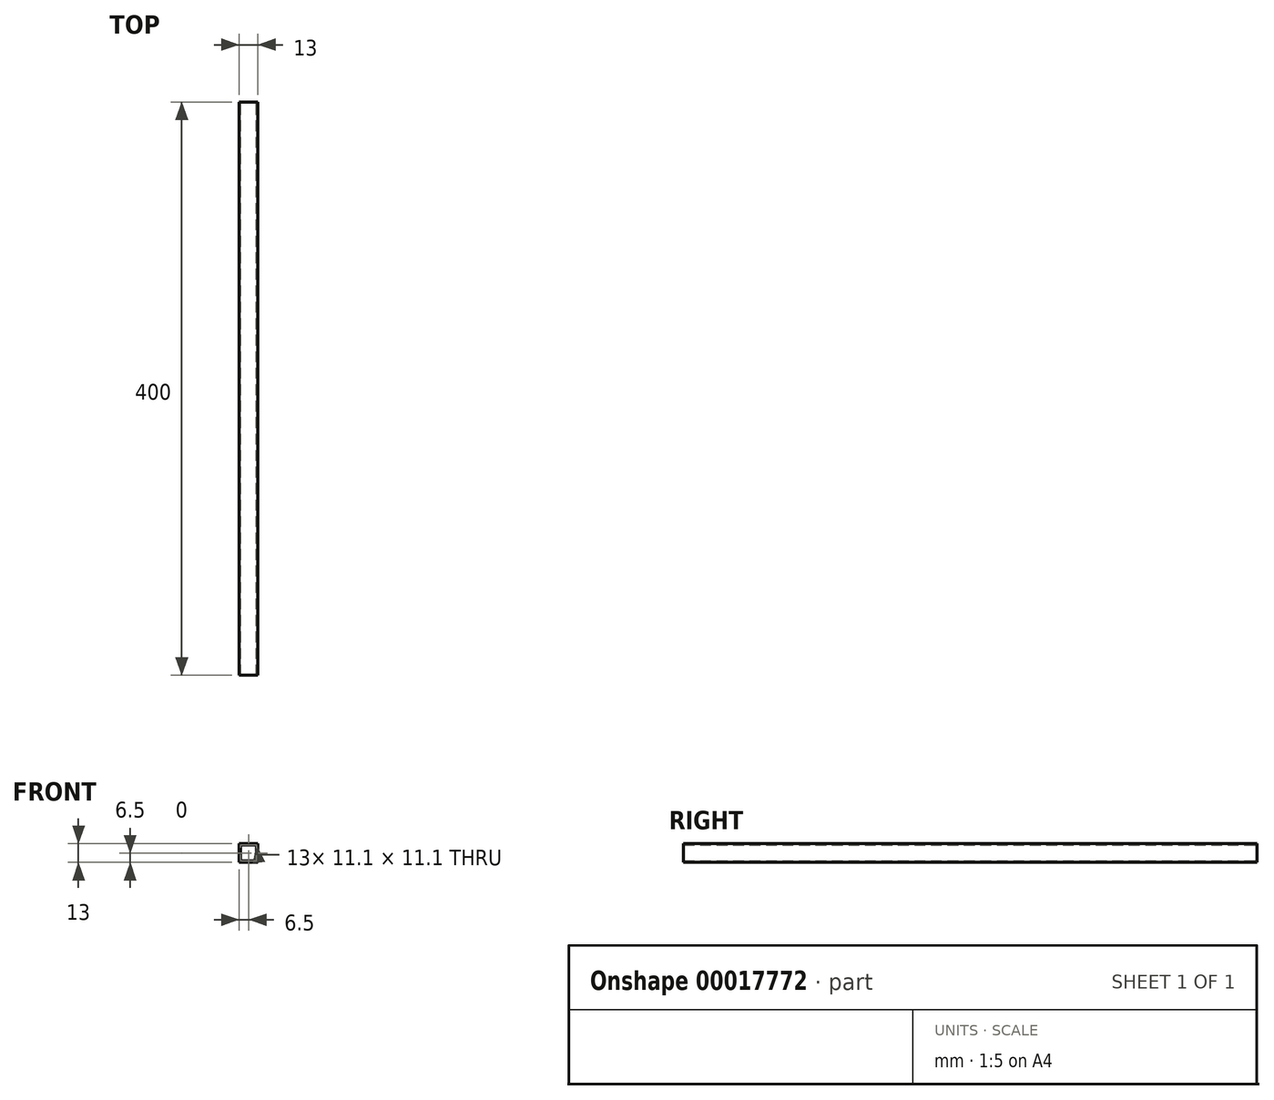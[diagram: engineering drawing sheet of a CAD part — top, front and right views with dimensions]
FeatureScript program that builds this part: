
annotation { "Feature Type Name" : "Feature", "Feature Type Description" : "" }
export const myFeature = defineFeature(function(context is Context, id is Id, definition is map)
    precondition{}
    {
        {
            var Q0;
            Q0=qCreatedBy(makeId("Front.planeOp"),FACE);
            var sketch = newSketch(context, id + "F0", { "sketchPlane" : qUnion([Q0])});
            skLineSegment(sketch, "E0.rect.bottom", {"start": v(6.5, 6.5) * mm, "end": v(-6.5, 6.5) * mm});
            skLineSegment(sketch, "E0.rect.top", {"start": v(6.5, -6.5) * mm, "end": v(-6.5, -6.5) * mm});
            skLineSegment(sketch, "E0.rect.left", {"start": v(6.5, 6.5) * mm, "end": v(6.5, -6.5) * mm});
            skLineSegment(sketch, "E0.rect.right", {"start": v(-6.5, 6.5) * mm, "end": v(-6.5, -6.5) * mm});
            skPoint(sketch, "E0.rect.middle", {"position": v(0, 0) * mm});
            skLineSegment(sketch, "E1.0", {"start": v(-5.55, 5.55) * mm, "end": v(-5.55, -5.55) * mm});
            skLineSegment(sketch, "E1.1", {"start": v(5.55, 5.55) * mm, "end": v(-5.55, 5.55) * mm});
            skLineSegment(sketch, "E1.2", {"start": v(5.55, 5.55) * mm, "end": v(5.55, -5.55) * mm});
            skLineSegment(sketch, "E1.3", {"start": v(5.55, -5.55) * mm, "end": v(-5.55, -5.55) * mm});
            skSolve(sketch);
        }
        {
            var Q0;
            Q0=makeQuery(id+"F0.imprint","IMPRINT",FACE,{"disambiguationData":[TD([[makeQuery(id+"F0.imprint","IMPRINT",EDGE,{"derivedFrom":sQuery(id+"F0.wireOp",EDGE,"E0.rect.bottom")}),1.0]])]});
            extrude(context, id + "F1", {"entities" : qUnion([Q0]), "depth" : 400 * mm});
        }
    });
